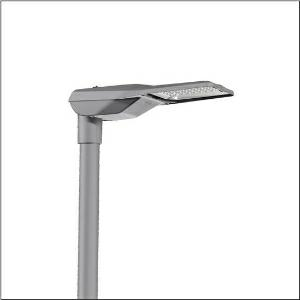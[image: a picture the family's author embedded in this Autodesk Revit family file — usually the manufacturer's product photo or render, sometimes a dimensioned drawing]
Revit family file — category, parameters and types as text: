
# Revit family: streetlight_sl_21_mini___st1_0ab_5xe2m33s08jb_1c43
name_source: partatom
category: Lighting Fixtures
units: mm (PartAtom-declared; Revit-internal decimal feet)

## family parameters
Cut with Voids When Loaded = No
Host = Face
Light Source = No
Part Type = Normal
Room Calculation Point = No
Round Connector Dimension = Use Diameter
Shared = No

## types (1)
- --- (1 x LED, 11390 lm, 88.6 W, 3000K)
    Apparent Load = 89 VA
    CIE Flux Codes = 40 74 97 100 100
    Color Rendering = 70
    Color Temperature = 3000K
    Default Elevation = 1800 mm
    Description = Streetlight SL 21 mini, mast luminaire, primary light control with lens, of PMMA, primary optical cover: cover, of toughened safety glass, transparent, light distribution: ST1.0aB, light emission: direct distribution, primary light characteristic: asymmetric, installation type: side-entry, post-top, LED, High Power LED, rated luminous flux: 11.390lm, luminous efficacy: 129lm/W, light colour: 730, colour temperature: 3000K, control gear: D4i, control: flexible luminous flux parameterisation, time-dependent luminous flux control, constant luminous flux control, overheat protection, pre-setting: logarithmic dimming characteristic, mains connection: 220..240V, AC, 50/60Hz, start of lifetime: 89W, end of service life: 92W, reduction: 41W, luminaire housing, of diecast aluminium, powder-coated, SITECO metallic grey (DB 702S), corrosivity category C5 high according to DIN EN ISO 12944, please order mast flange separately, inclination adjustable: 0°, 5°, 10°, 15°, sealing non-destructively replaceable, multi-level sealing system, length: 628mm, width: 235mm, height: 110mm, mast flange for spigot size: 42mm (side-entry): 5XC10008XM4, 60/48mm (side-entry/post-top): 5XC10108XM2, 76/60mm (side-entry/post-top): 5XC10108XM1, mounting height: 4..8m, Smart Interface above, protection rating (complete): IP66, insulation class (complete): insulation class II (safety insulation), certification: CE, ENEC, ENEC+, VDE, impact resistance: IK10, permissible operating ambient temperature for outdoor applications: -40..+50°C, standard-compliant lighting for roads and squares, packaging unit: 1 piece

Light Distribution: ST1.0aB
    Height = 110 mm
    Lamp = 1 x LED
    Lamp Light Flux = 11390 lm
    Lamp Power = 88.6 W
    Lamp count = 1
    Length = 625 mm
    Luminous efficacy = 129 lm/W
    Manufacturer = Siteco
    ModVariant = No
    Model = 5XE2M33S08JB
    Number of Poles = 1
    OnlyDefault = Yes
    Power Factor = 1
    Product Name = Streetlight SL 21 mini | ST1.0aB
    Product group = mast luminaire | pylon top
    ProductGroupID = 6100
    Protection Class = Protection class II
    Protection Degree = IP 66
    RLX_Detail_Level = 1
    RLX_Emergency_Light_Flux = 0 lm
    RLX_Emergency_Type = 0
    RLX_Emergency_Type_DB = No
    RlxData = <blob elided: 26177 chars, md5=f3e7b7b6>
    Socket = socket
    Standby Power = 0 W
    System Light Flux = 11390 lm
    System Power = 89 W
    Type Comments = factory setting: luminous flux: 100 % | dim-lin: 254 | 915 mA
    Type Image = l_1003515.jpg
    URL = http://relux.com
    VarID = @adj_030513
    Voltage = 0 V
    Weight = 0.00 kg
    Width = 234 mm

## geometry (parser evidence)
native form markers: Blend x4, Sweep x12
no freeform markers — native parametric forms only
